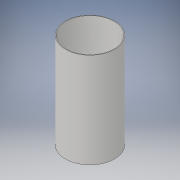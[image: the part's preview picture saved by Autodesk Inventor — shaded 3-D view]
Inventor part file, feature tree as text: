
AUTODESK INVENTOR PART (.ipt)
format: ipt  version: 2017 (Build 210142000, 142)  size: 94,720 bytes
history: native  units: in
note: dims shown in document units (in); Inventor stores cm internally (conversion verified against a paired STEP export)
features: extrude x1, sketch x1
ambient origin geometry x8: Origin, YZ Plane, XZ Plane, XY Plane, X Axis, Y Axis, Z Axis, Center Point
bodies: Solid1 (feature_tree)
feature tree (2):
  extrude  "Extrusion1"  Depth=14.0in
  sketch  "Sketch1"  dims[d0=7.25in d1=7.062in d2=14.0in d3=0.0in]
